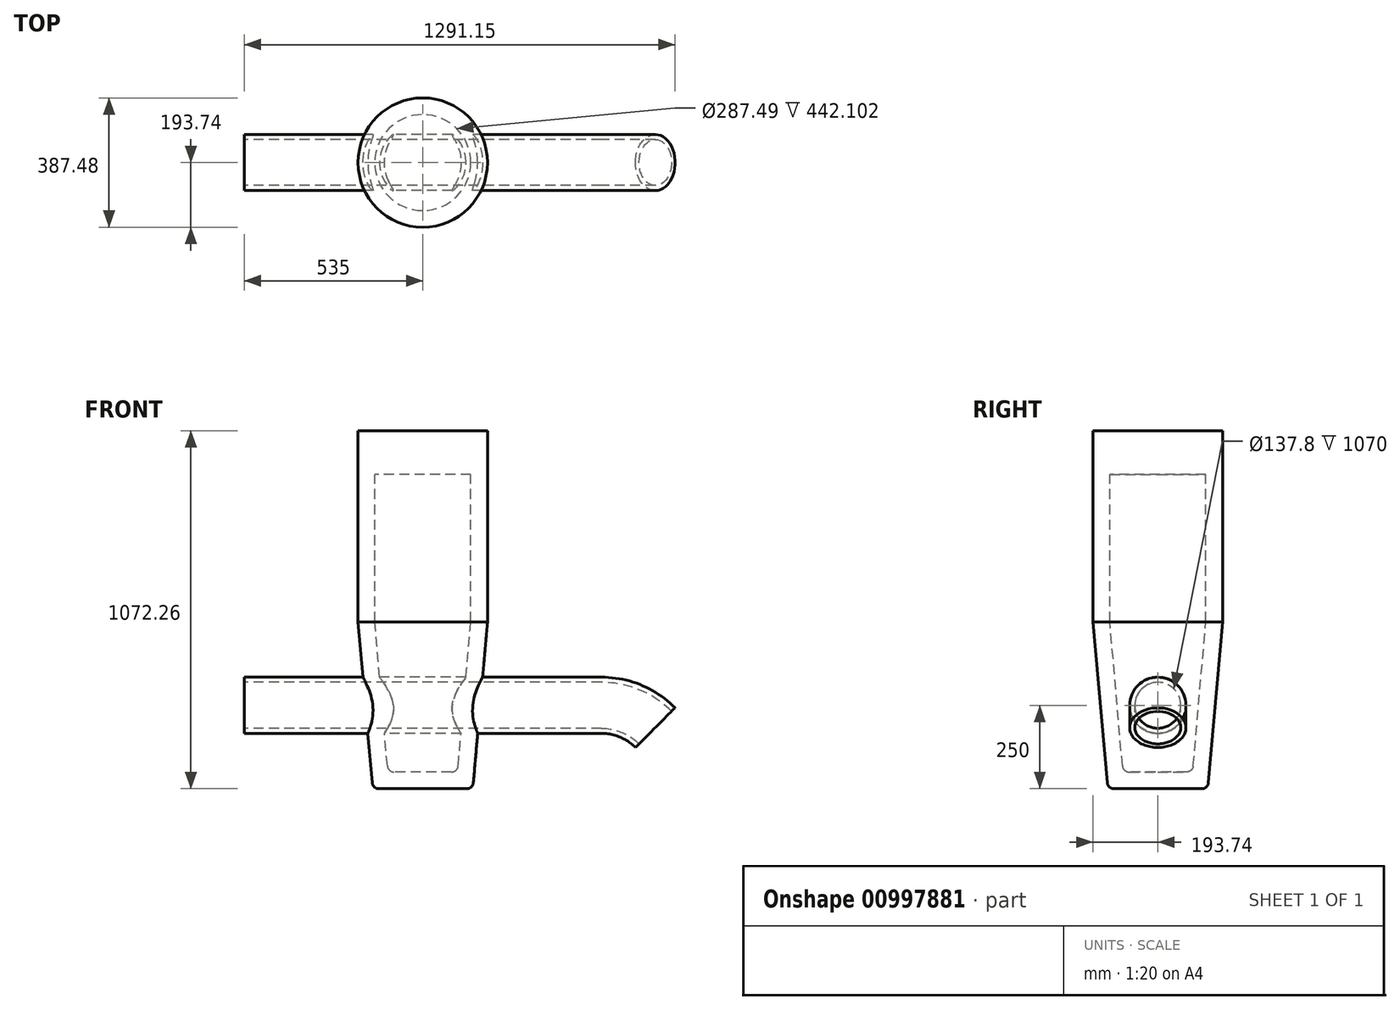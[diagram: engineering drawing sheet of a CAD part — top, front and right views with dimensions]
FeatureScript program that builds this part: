
annotation { "Feature Type Name" : "Feature", "Feature Type Description" : "" }
export const myFeature = defineFeature(function(context is Context, id is Id, definition is map)
    precondition{}
    {
        {
            var Q0;
            Q0=qCreatedBy(makeId("Front.planeOp"),FACE);
            var sketch = newSketch(context, id + "F0", { "sketchPlane" : qUnion([Q0])});
            skLineSegment(sketch, "E0", {"start": v(0, 0) * mm, "end": v(0, -50) * mm});
            skLineSegment(sketch, "E1", {"start": v(0, -50) * mm, "end": v(131.67, -50) * mm});
            skLineSegment(sketch, "E2", {"start": v(151.6, -31.74) * mm, "end": v(193.74, 450) * mm});
            skLineSegment(sketch, "E3", {"start": v(143.74, 450) * mm, "end": v(105.97, 18.26) * mm});
            skLineSegment(sketch, "E4", {"start": v(86.05, 0) * mm, "end": v(0, 0) * mm});
            skPoint(sketch, "E5.visualSharp", {"position": v(150, -50) * mm});
            skArc(sketch, "E5.filletArc", {"start": v(131.67, -50) * mm, "mid": v(145.19, -44.75) * mm, "end": v(151.6, -31.74) * mm});
            skPoint(sketch, "E6.visualSharp", {"position": v(104.37, 0) * mm});
            skArc(sketch, "E6.filletArc", {"start": v(86.05, 0) * mm, "mid": v(99.56, 5.25) * mm, "end": v(105.97, 18.26) * mm});
            skLineSegment(sketch, "E7", {"start": v(193.74, 1022.26) * mm, "end": v(193.74, 450) * mm});
            skLineSegment(sketch, "E8", {"start": v(193.74, 1022.26) * mm, "end": v(0, 1022.26) * mm});
            skLineSegment(sketch, "E9", {"start": v(0, 1022.26) * mm, "end": v(0, 892.1) * mm});
            skLineSegment(sketch, "E10", {"start": v(0, 892.1) * mm, "end": v(143.74, 892.1) * mm});
            skLineSegment(sketch, "E11", {"start": v(143.74, 892.1) * mm, "end": v(143.74, 450) * mm});
            skSolve(sketch);
        }
        {
            var Q0;
            Q0=makeQuery(id+"F0.imprint","IMPRINT",FACE,{"disambiguationData":[TD([[makeQuery(id+"F0.imprint","IMPRINT",EDGE,{"derivedFrom":sQuery(id+"F0.wireOp",EDGE,"E0")}),1.0]])]});
            var Q1;
            Q1=sQuery(id+"F0.wireOp",EDGE,"E0");
            revolve(context, id + "F1", {"surfaceOperationType" : NewSurfaceOperationType.NEW, "entities" : qUnion([Q0]), "axis" : qUnion([Q1]), "revolveType" : RevolveType.FULL});
        }
        {
            var Q0;
            Q0=qCreatedBy(makeId("Right.planeOp"),FACE);
            var sketch = newSketch(context, id + "F2", { "sketchPlane" : qUnion([Q0])});
            skCircle(sketch, "E12", {"center": v(0, 200) * mm, "radius": 84.15 * mm});
            skSolve(sketch);
        }
        {
            var Q0;
            Q0=makeQuery(id+"F2.imprint","IMPRINT",FACE,{"disambiguationData":[TD([[makeQuery(id+"F2.imprint","IMPRINT",EDGE,{"derivedFrom":sQuery(id+"F2.wireOp",EDGE,"E12")}),1.0]])]});
            extrude(context, id + "F3", {"entities" : qUnion([Q0]), "operationType" : NewBodyOperationType.ADD, "endBound" : BoundingType.SYMMETRIC, "depth" : 1070 * mm, "offsetDistance" : 25 * mm});
        }
        {
            var Q0;
            Q0=makeQuery(id+"F3.opExtrude","CAP_FACE",FACE,{"disambiguationData":[OSD([sQuery(id+"F2.wireOp",EDGE,"E12")])],"isStart":true});
            var sketch = newSketch(context, id + "F4", { "sketchPlane" : qUnion([Q0])});
            skCircle(sketch, "E13", {"center": v(0, 200) * mm, "radius": 68.9 * mm});
            skSolve(sketch);
        }
        {
            var Q0;
            Q0=sQuery(id+"F4.wireOp",VERTEX,"E13.center");
            var Q1;
            Q1=makeQuery(id+"F1.opRevolve","SWEPT_BODY",BODY,{"disambiguationData":[OSD([sQuery(id+"F0.wireOp",EDGE,"E0"),sQuery(id+"F0.wireOp",EDGE,"E1"),sQuery(id+"F0.wireOp",EDGE,"E2"),sQuery(id+"F0.wireOp",EDGE,"5KsbOU5s-5Irl-RegO-nbgt-elMtKiIE67k7"),sQuery(id+"F0.wireOp",EDGE,"E3"),sQuery(id+"F0.wireOp",EDGE,"E4"),sQuery(id+"F0.wireOp",EDGE,"E5.filletArc"),sQuery(id+"F0.wireOp",EDGE,"E6.filletArc")])]});
            hole(context, id + "F5", {"style" : HoleStyle.SIMPLE, "endStyle" : HoleEndStyle.THROUGH, "holeDiameter" : 137.8 * mm, "majorDiameter" : 5 * mm, "isTappedThrough" : true, "tappedDepth" : 12 * mm, "tapClearance" : 3, "locations" : qUnion([Q0]), "scope" : qUnion([Q1])});
        }
        {
            var Q0;
            Q0=sQuery(id+"F0.wireOp",EDGE,"E2");
            cPlane(context, id + "F6", {"entities" : qUnion([Q0]), "cplaneType" : CPlaneType.LINE_ANGLE, "offset" : 25 * mm, "angle" : 90 * degree, "width" : 150 * mm, "height" : 150 * mm});
        }
        {
            var Q0;
            Q0=qCreatedBy(id+"F6.planeOp",FACE);
            var sketch = newSketch(context, id + "F7", { "sketchPlane" : qUnion([Q0])});
            skLineSegment(sketch, "E14.0", {"start": v(-535, 268.9) * mm, "end": v(-535, 131.1) * mm, "construction": true});
            skLineSegment(sketch, "E15.0", {"start": v(-535, 115.85) * mm, "end": v(-535, 284.15) * mm, "construction": true});
            skLineSegment(sketch, "E16", {"start": v(-535, 115.85) * mm, "end": v(-535, -28.6) * mm, "construction": true});
            skArc(sketch, "E17", {"start": v(-535, 200) * mm, "mid": v(-622.48, 182.6) * mm, "end": v(-696.64, 133.04) * mm});
            skLineSegment(sketch, "E18", {"start": v(-696.64, 133.04) * mm, "end": v(-535, -28.6) * mm, "construction": true});
            skSolve(sketch);
        }
        {
            var Q0;
            Q0=makeQuery(id+"F3.opExtrude","CAP_FACE",FACE,{"disambiguationData":[OSD([sQuery(id+"F2.wireOp",EDGE,"E12")])],"isStart":false});
            var Q1;
            Q1=sQuery(id+"F7.wireOp",EDGE,"E17");
            sweep(context, id + "F8", {"operationType" : NewBodyOperationType.ADD, "profiles" : qUnion([Q0]), "path" : qUnion([Q1])});
        }
    });
